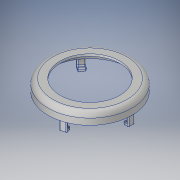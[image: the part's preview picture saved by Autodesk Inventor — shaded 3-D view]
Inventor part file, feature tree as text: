
AUTODESK INVENTOR PART (.ipt)
format: ipt  version: 2018 (Build 220112000, 112)  size: 286,208 bytes
history: native  units: in
note: dims shown in document units (in); Inventor stores cm internally (conversion verified against a paired STEP export)
features: extrude x3, sketch x3, fillet x2, shell x1, pattern_circular x1
ambient origin geometry x8: Origin, YZ Plane, XZ Plane, XY Plane, X Axis, Y Axis, Z Axis, Center Point
bodies: Solid1 (feature_tree)
feature tree (10):
  extrude  "Extrusion1"  Depth=0.0175in
  shell  "Shell1"  Thickness=0.09in
  fillet  "Fillet1"  Radius=0.0175in
  extrude  "Extrusion2"  Depth=0.075in TaperAngle=0.0deg
  extrude  "Extrusion3"  Depth=0.0075in
  fillet  "Fillet2"  Radius=1.9685in
  pattern_circular  "Circular Pattern1"  [2 undecoded]
  sketch  "Sketch1"  dims[d0=0.48in d1=0.675in d2=0.09in d3=0.0in d4=0.0175in]
  sketch  "Sketch2"  dims[d5=0.04in d6=0.075in d7=0.0in]
  sketch  "Sketch3"  dims[d8=0.0255in d9=0.0in d10=0.0075in d11=1.9685in d12=360.0deg]
note: 2 required parameter values undecoded (feature->parameter linkage not recoverable at this tier; creation-order binding heuristic only, values carry confidence <= 0.55)
